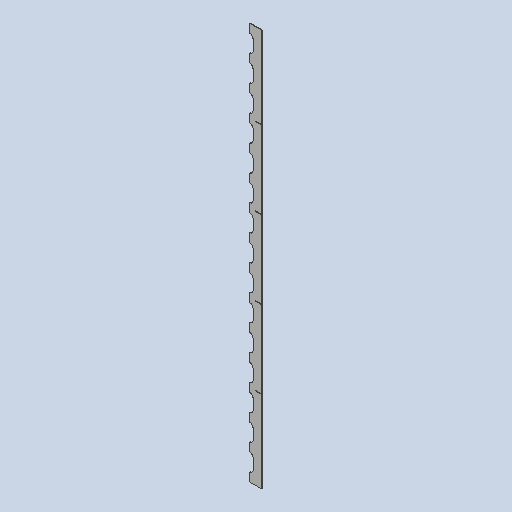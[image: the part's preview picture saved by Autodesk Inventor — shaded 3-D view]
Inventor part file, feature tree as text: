
AUTODESK INVENTOR PART (.ipt)
format: ipt  version: 2025 (Build 290162010, 162A)  size: 256,000 bytes
history: native  units: mm
features: sketch x3, extrude x2, other x2, sheet_metal_op x1, pattern_linear x1, projected_geometry x1
ambient origin geometry x8: Origin, YZ Plane, XZ Plane, XY Plane, X Axis, Y Axis, Z Axis, Center Point
bodies: Body1 (feature_tree)
feature tree (10):
  sheet_metal_op  "Face2"
  extrude  "Extrusion2"  Depth=2300.0mm
  pattern_linear  "Rectangular Pattern2"  Count1=2  [1 undecoded]
  extrude  "Extrusion3"  Depth=450.0mm
  sketch  "Sketch6"  dims[d26=70.28909mm d27=2300.0mm]
  other  "Plate4"
  sketch  "Sketch7"  dims[d28=3.0mm]
  projected_geometry  "Projected Loop1"
  sketch  "Sketch8"  dims[d32=0.0mm d33=0.0mm d37=20.0mm d38=100.0mm d39=150.0mm d41=150.0mm d42=3.2mm d44=36.0mm d45=225.0mm d46=36.0mm d47=3.2mm d48=450.0mm d49=36.0mm d50=36.0mm d51=3.2mm d52=3.2mm d53=225.0mm d54=450.0mm d55=0.0mm d56=0.0mm]
  other  "Definition1"
note: 1 required parameter value undecoded (feature->parameter linkage not recoverable at this tier; creation-order binding heuristic only, values carry confidence <= 0.55)
